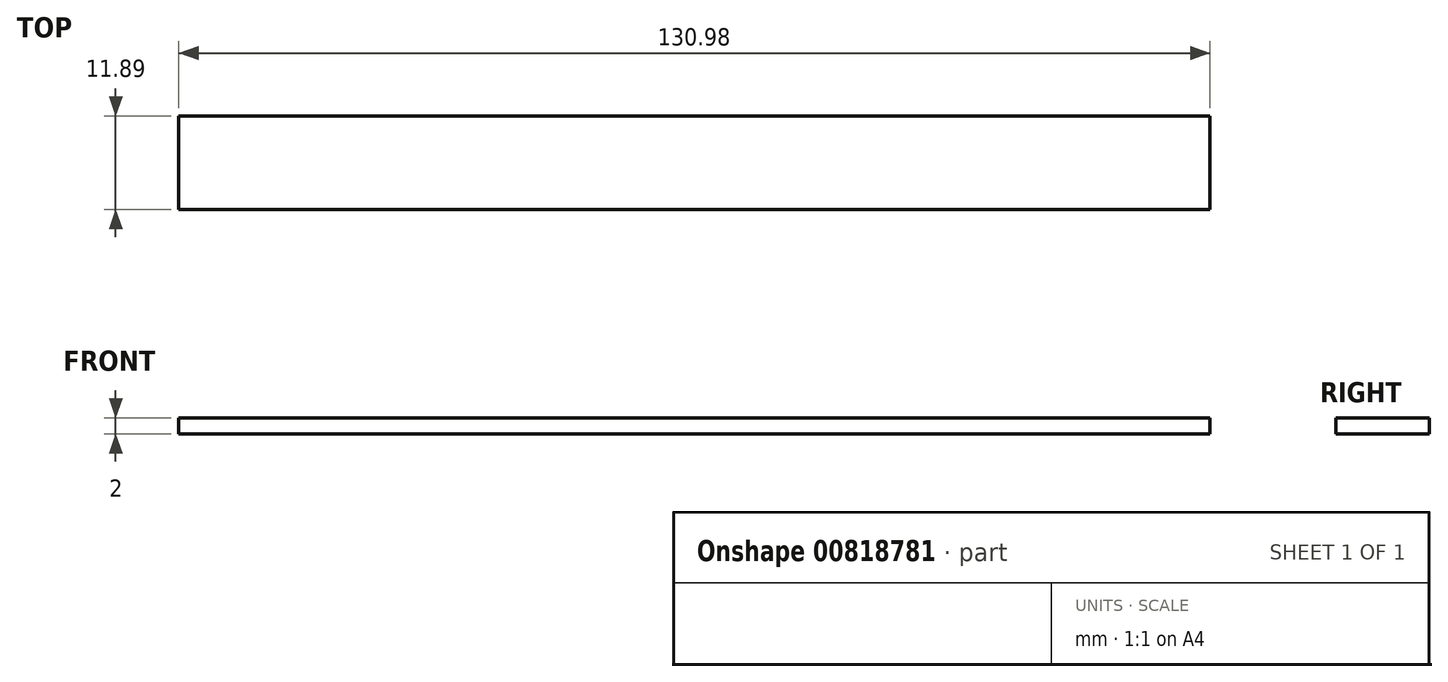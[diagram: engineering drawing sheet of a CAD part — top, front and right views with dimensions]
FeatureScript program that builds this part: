
annotation { "Feature Type Name" : "Feature", "Feature Type Description" : "" }
export const myFeature = defineFeature(function(context is Context, id is Id, definition is map)
    precondition{}
    {
        {
            var Q0;
            Q0=qCreatedBy(makeId("Top.planeOp"),FACE);
            var sketch = newSketch(context, id + "F0", { "sketchPlane" : qUnion([Q0])});
            skLineSegment(sketch, "E0.bottom", {"start": v(-56.37, -17) * mm, "end": v(74.6, -17) * mm});
            skLineSegment(sketch, "E0.top", {"start": v(-56.37, -28.88) * mm, "end": v(74.6, -28.88) * mm});
            skLineSegment(sketch, "E0.left", {"start": v(-56.37, -17) * mm, "end": v(-56.37, -28.88) * mm});
            skLineSegment(sketch, "E0.right", {"start": v(74.6, -17) * mm, "end": v(74.6, -28.88) * mm});
            skSolve(sketch);
        }
        {
            var Q0;
            Q0=makeQuery(id+"F0.imprint","IMPRINT",FACE,{"disambiguationData":[TD([[makeQuery(id+"F0.imprint","IMPRINT",EDGE,{"derivedFrom":sQuery(id+"F0.wireOp",EDGE,"E0.bottom")}),-1.0]])]});
            extrude(context, id + "F1", {"entities" : qUnion([Q0]), "depth" : 2 * mm, "offsetDistance" : 25 * mm});
        }
    });
